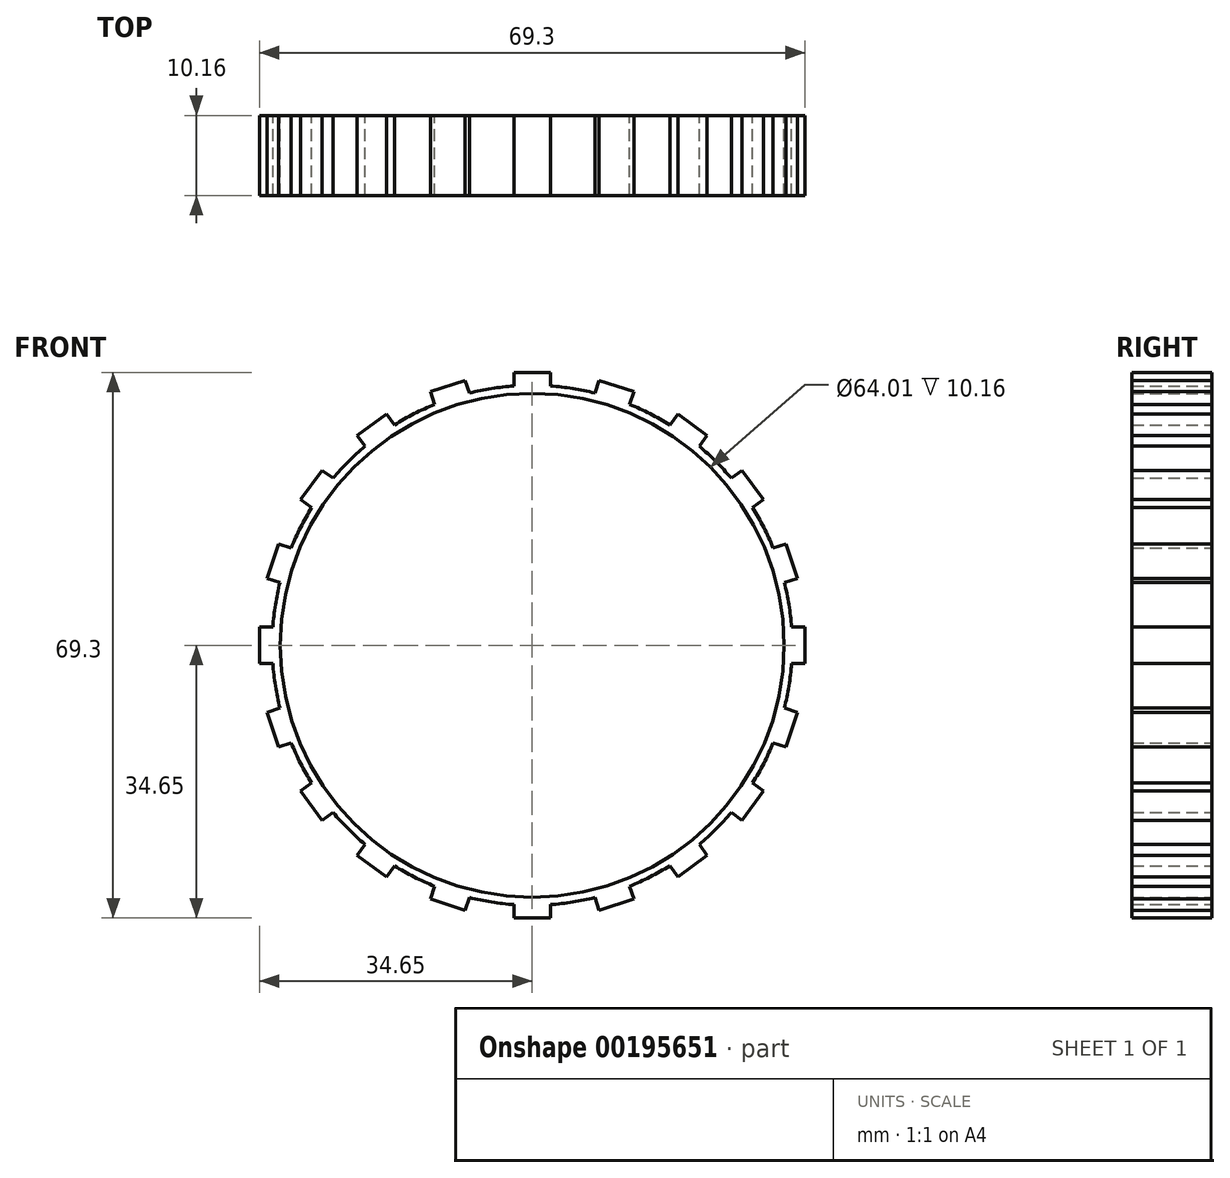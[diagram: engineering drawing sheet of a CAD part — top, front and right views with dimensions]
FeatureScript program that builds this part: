
annotation { "Feature Type Name" : "Feature", "Feature Type Description" : "" }
export const myFeature = defineFeature(function(context is Context, id is Id, definition is map)
    precondition{}
    {
        {
            var Q0;
            Q0=qCreatedBy(makeId("Front.planeOp"),FACE);
            var sketch = newSketch(context, id + "F0", { "sketchPlane" : qUnion([Q0])});
            skCircle(sketch, "E0", {"center": v(0, 0) * mm, "radius": 33.02 * mm});
            skCircle(sketch, "E1", {"center": v(0, 0) * mm, "radius": 32 * mm});
            skLineSegment(sketch, "E2.bottom", {"start": v(-2.3, 34.65) * mm, "end": v(2.3, 34.65) * mm});
            skLineSegment(sketch, "E2.left", {"start": v(-2.3, 34.65) * mm, "end": v(-2.3, 32.94) * mm});
            skLineSegment(sketch, "E2.right", {"start": v(2.3, 34.65) * mm, "end": v(2.3, 32.94) * mm});
            skPoint(sketch, "E2.middle", {"position": v(0, 33.02) * mm});
            skLineSegment(sketch, "E3.trimOffspring", {"start": v(2.3, 31.92) * mm, "end": v(2.3, 31.4) * mm});
            skLineSegment(sketch, "E4.trimOffspring", {"start": v(-2.3, 31.92) * mm, "end": v(-2.3, 31.4) * mm});
            skLineSegment(sketch, "E5.1.0", {"start": v(-12.9, 32.24) * mm, "end": v(-12.37, 30.61) * mm});
            skLineSegment(sketch, "E5.1.1", {"start": v(-12.9, 32.24) * mm, "end": v(-8.51, 33.67) * mm});
            skLineSegment(sketch, "E5.1.2", {"start": v(-8.51, 33.67) * mm, "end": v(-7.98, 32.04) * mm});
            skLineSegment(sketch, "E5.2.0", {"start": v(-22.23, 26.68) * mm, "end": v(-21.23, 25.3) * mm});
            skLineSegment(sketch, "E5.2.1", {"start": v(-22.23, 26.68) * mm, "end": v(-18.5, 29.39) * mm});
            skLineSegment(sketch, "E5.2.2", {"start": v(-18.5, 29.39) * mm, "end": v(-17.5, 28) * mm});
            skLineSegment(sketch, "E6.2.3.0", {"start": v(-29.39, 18.5) * mm, "end": v(-28, 17.5) * mm});
            skLineSegment(sketch, "E6.3.3.0", {"start": v(-29.39, 18.5) * mm, "end": v(-26.68, 22.23) * mm});
            skLineSegment(sketch, "E6.6.3.0", {"start": v(-26.68, 22.23) * mm, "end": v(-25.3, 21.23) * mm});
            skLineSegment(sketch, "E6.2.4.0", {"start": v(-33.67, 8.51) * mm, "end": v(-32.04, 7.98) * mm});
            skLineSegment(sketch, "E6.3.4.0", {"start": v(-33.67, 8.51) * mm, "end": v(-32.24, 12.9) * mm});
            skLineSegment(sketch, "E6.6.4.0", {"start": v(-32.24, 12.9) * mm, "end": v(-30.61, 12.37) * mm});
            skLineSegment(sketch, "E6.2.5.0", {"start": v(-34.65, -2.3) * mm, "end": v(-32.94, -2.3) * mm});
            skLineSegment(sketch, "E6.3.5.0", {"start": v(-34.65, -2.3) * mm, "end": v(-34.65, 2.3) * mm});
            skLineSegment(sketch, "E6.6.5.0", {"start": v(-34.65, 2.3) * mm, "end": v(-32.94, 2.3) * mm});
            skLineSegment(sketch, "E6.2.6.0", {"start": v(-32.24, -12.9) * mm, "end": v(-30.61, -12.37) * mm});
            skLineSegment(sketch, "E6.3.6.0", {"start": v(-32.24, -12.9) * mm, "end": v(-33.67, -8.51) * mm});
            skLineSegment(sketch, "E6.6.6.0", {"start": v(-33.67, -8.51) * mm, "end": v(-32.04, -7.98) * mm});
            skLineSegment(sketch, "E6.2.7.0", {"start": v(-26.68, -22.23) * mm, "end": v(-25.3, -21.23) * mm});
            skLineSegment(sketch, "E6.3.7.0", {"start": v(-26.68, -22.23) * mm, "end": v(-29.39, -18.5) * mm});
            skLineSegment(sketch, "E6.6.7.0", {"start": v(-29.39, -18.5) * mm, "end": v(-28, -17.5) * mm});
            skLineSegment(sketch, "E6.2.8.0", {"start": v(-18.5, -29.39) * mm, "end": v(-17.5, -28) * mm});
            skLineSegment(sketch, "E6.3.8.0", {"start": v(-18.5, -29.39) * mm, "end": v(-22.23, -26.68) * mm});
            skLineSegment(sketch, "E6.6.8.0", {"start": v(-22.23, -26.68) * mm, "end": v(-21.23, -25.3) * mm});
            skLineSegment(sketch, "E6.2.9.0", {"start": v(-8.51, -33.67) * mm, "end": v(-7.98, -32.04) * mm});
            skLineSegment(sketch, "E6.3.9.0", {"start": v(-8.51, -33.67) * mm, "end": v(-12.9, -32.24) * mm});
            skLineSegment(sketch, "E6.6.9.0", {"start": v(-12.9, -32.24) * mm, "end": v(-12.37, -30.61) * mm});
            skLineSegment(sketch, "E6.2.10.0", {"start": v(2.3, -34.65) * mm, "end": v(2.3, -32.94) * mm});
            skLineSegment(sketch, "E6.3.10.0", {"start": v(2.3, -34.65) * mm, "end": v(-2.3, -34.65) * mm});
            skLineSegment(sketch, "E6.6.10.0", {"start": v(-2.3, -34.65) * mm, "end": v(-2.3, -32.94) * mm});
            skLineSegment(sketch, "E6.2.11.0", {"start": v(12.9, -32.24) * mm, "end": v(12.37, -30.61) * mm});
            skLineSegment(sketch, "E6.3.11.0", {"start": v(12.9, -32.24) * mm, "end": v(8.51, -33.67) * mm});
            skLineSegment(sketch, "E6.6.11.0", {"start": v(8.51, -33.67) * mm, "end": v(7.98, -32.04) * mm});
            skLineSegment(sketch, "E6.2.12.0", {"start": v(22.23, -26.68) * mm, "end": v(21.23, -25.3) * mm});
            skLineSegment(sketch, "E6.3.12.0", {"start": v(22.23, -26.68) * mm, "end": v(18.5, -29.39) * mm});
            skLineSegment(sketch, "E6.6.12.0", {"start": v(18.5, -29.39) * mm, "end": v(17.5, -28) * mm});
            skLineSegment(sketch, "E6.2.13.0", {"start": v(29.39, -18.5) * mm, "end": v(28, -17.5) * mm});
            skLineSegment(sketch, "E6.3.13.0", {"start": v(29.39, -18.5) * mm, "end": v(26.68, -22.23) * mm});
            skLineSegment(sketch, "E6.6.13.0", {"start": v(26.68, -22.23) * mm, "end": v(25.3, -21.23) * mm});
            skLineSegment(sketch, "E6.2.14.0", {"start": v(33.67, -8.51) * mm, "end": v(32.04, -7.98) * mm});
            skLineSegment(sketch, "E6.3.14.0", {"start": v(33.67, -8.51) * mm, "end": v(32.24, -12.9) * mm});
            skLineSegment(sketch, "E6.6.14.0", {"start": v(32.24, -12.9) * mm, "end": v(30.61, -12.37) * mm});
            skLineSegment(sketch, "E6.2.15.0", {"start": v(34.65, 2.3) * mm, "end": v(32.94, 2.3) * mm});
            skLineSegment(sketch, "E6.3.15.0", {"start": v(34.65, 2.3) * mm, "end": v(34.65, -2.3) * mm});
            skLineSegment(sketch, "E6.6.15.0", {"start": v(34.65, -2.3) * mm, "end": v(32.94, -2.3) * mm});
            skLineSegment(sketch, "E6.2.16.0", {"start": v(32.24, 12.9) * mm, "end": v(30.61, 12.37) * mm});
            skLineSegment(sketch, "E6.3.16.0", {"start": v(32.24, 12.9) * mm, "end": v(33.67, 8.51) * mm});
            skLineSegment(sketch, "E6.6.16.0", {"start": v(33.67, 8.51) * mm, "end": v(32.04, 7.98) * mm});
            skLineSegment(sketch, "E6.2.17.0", {"start": v(26.68, 22.23) * mm, "end": v(25.3, 21.23) * mm});
            skLineSegment(sketch, "E6.3.17.0", {"start": v(26.68, 22.23) * mm, "end": v(29.39, 18.5) * mm});
            skLineSegment(sketch, "E6.6.17.0", {"start": v(29.39, 18.5) * mm, "end": v(28, 17.5) * mm});
            skLineSegment(sketch, "E6.2.18.0", {"start": v(18.5, 29.39) * mm, "end": v(17.5, 28) * mm});
            skLineSegment(sketch, "E6.3.18.0", {"start": v(18.5, 29.39) * mm, "end": v(22.23, 26.68) * mm});
            skLineSegment(sketch, "E6.6.18.0", {"start": v(22.23, 26.68) * mm, "end": v(21.23, 25.3) * mm});
            skLineSegment(sketch, "E6.2.19.0", {"start": v(8.51, 33.67) * mm, "end": v(7.98, 32.04) * mm});
            skLineSegment(sketch, "E6.3.19.0", {"start": v(8.51, 33.67) * mm, "end": v(12.9, 32.24) * mm});
            skLineSegment(sketch, "E6.6.19.0", {"start": v(12.9, 32.24) * mm, "end": v(12.37, 30.61) * mm});
            skSolve(sketch);
        }
        {
            var Q0;
            {var subQ28=sQuery(id+"F0.wireOp",EDGE,"E1");var subQ29=makeQuery(id+"F0.imprint","IMPRINT",VERTEX,{"disambiguationData":[OD(0.0)],"derivedFrom":subQ28});Q0=makeQuery(id+"F0.imprint","IMPRINT",FACE,{"disambiguationData":[TD([[makeQuery(id+"F0.imprint","IMPRINT",EDGE,{"disambiguationData":[TD([[subQ29,-1.0]])],"derivedFrom":subQ28}),-1.0]])]});}
            var Q1;
            {var subQ0=sQuery(id+"F0.wireOp",EDGE,"E5.2.0");Q1=makeQuery(id+"F0.imprint","IMPRINT",FACE,{"disambiguationData":[TD([[makeQuery(id+"F0.imprint","IMPRINT",EDGE,{"derivedFrom":subQ0}),1.0]])]});}
            var Q2;
            {var subQ0=sQuery(id+"F0.wireOp",EDGE,"E6.2.3.0");Q2=makeQuery(id+"F0.imprint","IMPRINT",FACE,{"disambiguationData":[TD([[makeQuery(id+"F0.imprint","IMPRINT",EDGE,{"derivedFrom":subQ0}),1.0]])]});}
            var Q3;
            {var subQ0=sQuery(id+"F0.wireOp",EDGE,"E6.2.4.0");Q3=makeQuery(id+"F0.imprint","IMPRINT",FACE,{"disambiguationData":[TD([[makeQuery(id+"F0.imprint","IMPRINT",EDGE,{"derivedFrom":subQ0}),1.0]])]});}
            var Q4;
            {var subQ0=sQuery(id+"F0.wireOp",EDGE,"E6.2.5.0");Q4=makeQuery(id+"F0.imprint","IMPRINT",FACE,{"disambiguationData":[TD([[makeQuery(id+"F0.imprint","IMPRINT",EDGE,{"derivedFrom":subQ0}),1.0]])]});}
            var Q5;
            {var subQ0=sQuery(id+"F0.wireOp",EDGE,"E6.2.6.0");Q5=makeQuery(id+"F0.imprint","IMPRINT",FACE,{"disambiguationData":[TD([[makeQuery(id+"F0.imprint","IMPRINT",EDGE,{"derivedFrom":subQ0}),1.0]])]});}
            var Q6;
            {var subQ0=sQuery(id+"F0.wireOp",EDGE,"E6.2.7.0");Q6=makeQuery(id+"F0.imprint","IMPRINT",FACE,{"disambiguationData":[TD([[makeQuery(id+"F0.imprint","IMPRINT",EDGE,{"derivedFrom":subQ0}),1.0]])]});}
            var Q7;
            {var subQ0=sQuery(id+"F0.wireOp",EDGE,"E6.2.8.0");Q7=makeQuery(id+"F0.imprint","IMPRINT",FACE,{"disambiguationData":[TD([[makeQuery(id+"F0.imprint","IMPRINT",EDGE,{"derivedFrom":subQ0}),1.0]])]});}
            var Q8;
            {var subQ0=sQuery(id+"F0.wireOp",EDGE,"E6.2.9.0");Q8=makeQuery(id+"F0.imprint","IMPRINT",FACE,{"disambiguationData":[TD([[makeQuery(id+"F0.imprint","IMPRINT",EDGE,{"derivedFrom":subQ0}),1.0]])]});}
            var Q9;
            {var subQ0=sQuery(id+"F0.wireOp",EDGE,"E6.2.10.0");Q9=makeQuery(id+"F0.imprint","IMPRINT",FACE,{"disambiguationData":[TD([[makeQuery(id+"F0.imprint","IMPRINT",EDGE,{"derivedFrom":subQ0}),1.0]])]});}
            var Q10;
            {var subQ0=sQuery(id+"F0.wireOp",EDGE,"E6.2.11.0");Q10=makeQuery(id+"F0.imprint","IMPRINT",FACE,{"disambiguationData":[TD([[makeQuery(id+"F0.imprint","IMPRINT",EDGE,{"derivedFrom":subQ0}),1.0]])]});}
            var Q11;
            {var subQ0=sQuery(id+"F0.wireOp",EDGE,"E6.2.12.0");Q11=makeQuery(id+"F0.imprint","IMPRINT",FACE,{"disambiguationData":[TD([[makeQuery(id+"F0.imprint","IMPRINT",EDGE,{"derivedFrom":subQ0}),1.0]])]});}
            var Q12;
            {var subQ0=sQuery(id+"F0.wireOp",EDGE,"E6.2.13.0");Q12=makeQuery(id+"F0.imprint","IMPRINT",FACE,{"disambiguationData":[TD([[makeQuery(id+"F0.imprint","IMPRINT",EDGE,{"derivedFrom":subQ0}),1.0]])]});}
            var Q13;
            {var subQ0=sQuery(id+"F0.wireOp",EDGE,"E6.2.14.0");Q13=makeQuery(id+"F0.imprint","IMPRINT",FACE,{"disambiguationData":[TD([[makeQuery(id+"F0.imprint","IMPRINT",EDGE,{"derivedFrom":subQ0}),1.0]])]});}
            var Q14;
            {var subQ0=sQuery(id+"F0.wireOp",EDGE,"E6.2.15.0");Q14=makeQuery(id+"F0.imprint","IMPRINT",FACE,{"disambiguationData":[TD([[makeQuery(id+"F0.imprint","IMPRINT",EDGE,{"derivedFrom":subQ0}),1.0]])]});}
            var Q15;
            {var subQ0=sQuery(id+"F0.wireOp",EDGE,"E6.2.16.0");Q15=makeQuery(id+"F0.imprint","IMPRINT",FACE,{"disambiguationData":[TD([[makeQuery(id+"F0.imprint","IMPRINT",EDGE,{"derivedFrom":subQ0}),1.0]])]});}
            var Q16;
            {var subQ0=sQuery(id+"F0.wireOp",EDGE,"E6.2.17.0");Q16=makeQuery(id+"F0.imprint","IMPRINT",FACE,{"disambiguationData":[TD([[makeQuery(id+"F0.imprint","IMPRINT",EDGE,{"derivedFrom":subQ0}),1.0]])]});}
            var Q17;
            {var subQ0=sQuery(id+"F0.wireOp",EDGE,"E6.2.18.0");Q17=makeQuery(id+"F0.imprint","IMPRINT",FACE,{"disambiguationData":[TD([[makeQuery(id+"F0.imprint","IMPRINT",EDGE,{"derivedFrom":subQ0}),1.0]])]});}
            var Q18;
            {var subQ0=sQuery(id+"F0.wireOp",EDGE,"E6.2.19.0");Q18=makeQuery(id+"F0.imprint","IMPRINT",FACE,{"disambiguationData":[TD([[makeQuery(id+"F0.imprint","IMPRINT",EDGE,{"derivedFrom":subQ0}),1.0]])]});}
            var Q19;
            Q19=makeQuery(id+"F0.imprint","IMPRINT",FACE,{"disambiguationData":[TD([[makeQuery(id+"F0.imprint","IMPRINT",EDGE,{"derivedFrom":sQuery(id+"F0.wireOp",EDGE,"E2.bottom")}),-1.0]])]});
            var Q20;
            {var subQ0=sQuery(id+"F0.wireOp",EDGE,"E5.1.0");Q20=makeQuery(id+"F0.imprint","IMPRINT",FACE,{"disambiguationData":[TD([[makeQuery(id+"F0.imprint","IMPRINT",EDGE,{"derivedFrom":subQ0}),1.0]])]});}
            extrude(context, id + "F1", {"entities" : qUnion([Q0, Q1, Q2, Q3, Q4, Q5, Q6, Q7, Q8, Q9, Q10, Q11, Q12, Q13, Q14, Q15, Q16, Q17, Q18, Q19, Q20]), "depth" : 10.16 * mm});
        }
    });
